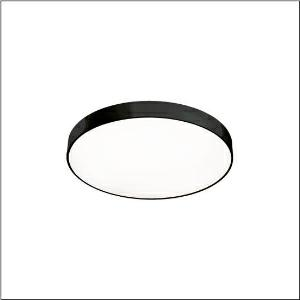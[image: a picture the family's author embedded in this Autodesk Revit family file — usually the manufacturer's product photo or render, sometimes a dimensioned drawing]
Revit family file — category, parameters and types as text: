
# Revit family: round_21_m_51mr36fm8321b
name_source: partatom
category: Lighting Fixtures
units: mm (PartAtom-declared; Revit-internal decimal feet)

## family parameters
Cut with Voids When Loaded = No
Host = Face
Light Source = No
Part Type = Normal
Room Calculation Point = No
Round Connector Dimension = Use Diameter
Shared = No

## types (1)
- --- (1 x LED, 7770 lm, 61.1 W, 3000K)
    Apparent Load = 61 VA
    CIE Flux Codes = 49 80 96 100 100
    Color Rendering = 80
    Color Temperature = 3000K
    Default Elevation = 1800 mm
    Description = Round 21 M, wall and ceiling luminaire, primary optical cover: cover, of PMMA, opal, light emission: direct distribution, primary light characteristic: symmetric, installation type: surface-mounted, suspended mounting, LED, rated luminous flux: 7.700lm, luminous efficacy: 127lm/W, light colour: 830, colour temperature: 3000K, with terminal, 3-pole, mains connection: 230V, AC, 50/60Hz, rated input power: 61W, housing, of aluminium, coated, black, diameter: 600mm, height: 62mm, protection rating (complete): IP40, insulation class (complete): insulation class I (protective earthing), certification: CE, impact resistance: IK04, permissible operating ambient temperature: -10..+35°C, packaging unit: 1 piece
    Height = 87 mm
    Lamp = 1 x LED
    Lamp Light Flux = 7770 lm
    Lamp Power = 61.1 W
    Lamp count = 1
    Length = 600 mm
    Luminous efficacy = 127 lm/W
    Manufacturer = Siteco
    ModVariant = No
    Model = 51MR36FM8321B
    Mounting Place = Ceiling
    Mounting Type = Surface mounted
    Number of Poles = 1
    OnlyDefault = Yes
    Power Factor = 1
    Product Name = Round 21 M
    Product group = wall and ceiling luminaire
    ProductGroupID = 302
    Protection Class = Protection class I
    Protection Degree = IP 40
    RLX_Detail_Level = 1
    RLX_Emergency_Light_Flux = 0 lm
    RLX_Emergency_Type = 0
    RLX_Emergency_Type_DB = No
    RlxData = <blob elided: 20361 chars, md5=da651964>
    Socket = socket
    Standby Power = 0 W
    System Light Flux = 7770 lm
    System Power = 61 W
    Type Comments = factory setting: luminous flux: 100 % | (ON | ON | ON | ON) | 700 mA
    Type Image = l_1258332.jpg
    URL = http://relux.com
    VarID = @adj_028575
    Voltage = 0 V
    Weight = 0.00 kg
    Width = 0 mm  [stored 0 ft]

note: [stored X ft] marks values corroborated as IEEE doubles in the binary element streams (Revit-internal decimal feet)

## geometry (parser evidence)
native form markers: Blend x4, Sweep x12
no freeform markers — native parametric forms only
